# Revit family: PLL - DELIVERY 1- PARTS
name_source: partatom
category: Generic Models
revit_build: Autodesk Revit 2017 (Build: 20160225_1515(x64)
units: mm (PartAtom-declared; Revit-internal decimal feet)

## family parameters
Always vertical = Yes
Can host rebar = No
Cut with Voids When Loaded = No
Part Type = Normal
Room Calculation Point = No
Round Connector Dimension = Use Diameter
Shared = No
Work Plane-Based = No

## types (3) — shared parameters
C_alteza da terra = 1000 mm  [stored 3.28084 ft]
C_spessore = 600 mm

## per-type parameters (varying)
| type | larghezza | profondità |
| 30x60cm | 300 mm  [stored 0.984252 ft] | 500 mm  [stored 1.64042 ft] |
| 50x60cm | 500 mm  [stored 1.64042 ft] | 500 mm  [stored 1.64042 ft] |
| 60x60cm | 600 mm | 600 mm |

note: [stored X ft] marks values corroborated as IEEE doubles in the binary element streams (Revit-internal decimal feet)

## geometry (parser evidence)
native form markers: Sweep x2
no freeform markers — native parametric forms only
